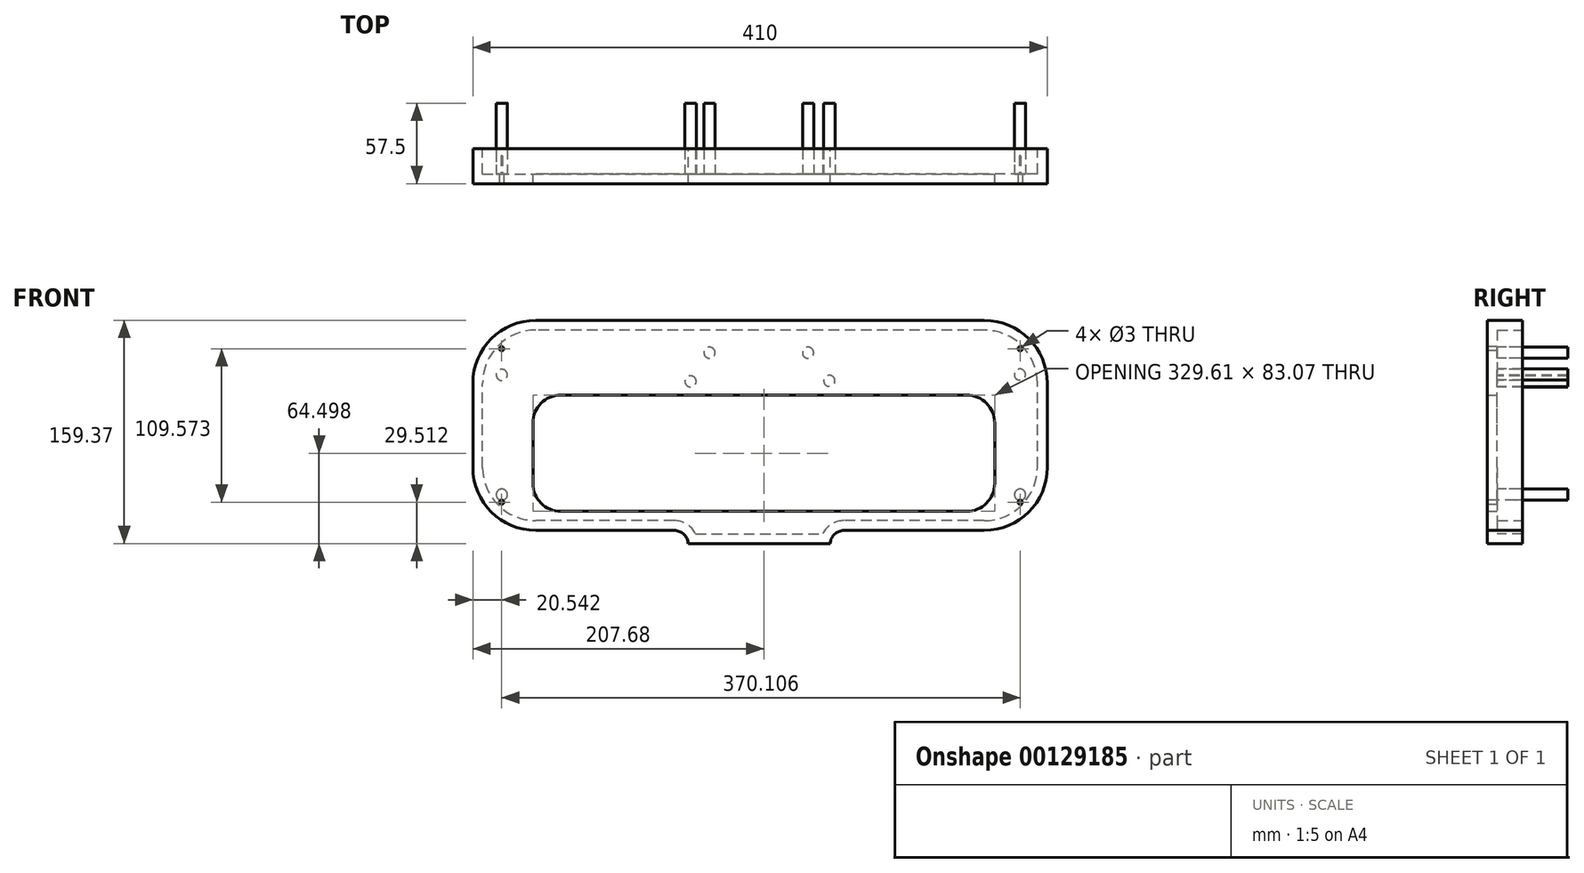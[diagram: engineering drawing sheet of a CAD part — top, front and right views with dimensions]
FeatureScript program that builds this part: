
annotation { "Feature Type Name" : "Feature", "Feature Type Description" : "" }
export const myFeature = defineFeature(function(context is Context, id is Id, definition is map)
    precondition{}
    {
        {
            var Q0;
            Q0=qCreatedBy(makeId("Front.planeOp"),FACE);
            var sketch = newSketch(context, id + "F0", { "sketchPlane" : qUnion([Q0])});
            skLineSegment(sketch, "E0.bottom", {"start": v(205, -75) * mm, "end": v(-205, -75) * mm});
            skLineSegment(sketch, "E0.top", {"start": v(205, 75) * mm, "end": v(-205, 75) * mm});
            skLineSegment(sketch, "E0.left", {"start": v(205, -75) * mm, "end": v(205, 75) * mm});
            skLineSegment(sketch, "E0.right", {"start": v(-205, -75) * mm, "end": v(-205, 75) * mm});
            skSolve(sketch);
        }
        {
            var Q0;
            Q0=qSketchRegion(id+"F0",true);
            extrude(context, id + "F1", {"entities" : qUnion([Q0]), "depth" : 5 * mm, "hasSecondDirection" : true, "secondDirectionOppositeDirection" : true, "secondDirectionDepth" : 20 * mm});
        }
        {
            var Q0;
            Q0=makeQuery(id+"F1.opExtrude","SWEPT_EDGE",EDGE,{"disambiguationData":[OSD([sQuery(id+"F0.wireOp",EDGE,"E0.top"),sQuery(id+"F0.wireOp",EDGE,"E0.right")])]});
            var Q1;
            Q1=makeQuery(id+"F1.opExtrude","SWEPT_EDGE",EDGE,{"disambiguationData":[OSD([sQuery(id+"F0.wireOp",EDGE,"E0.bottom"),sQuery(id+"F0.wireOp",EDGE,"E0.right")])]});
            fillet(context, id + "F2", {"entities" : qUnion([Q0, Q1]), "radius" : 45 * mm, "tangentPropagation" : true, "allowEdgeOverflow" : false});
        }
        {
            var Q0;
            Q0=makeQuery(id+"F1.opExtrude","SWEPT_EDGE",EDGE,{"disambiguationData":[OSD([sQuery(id+"F0.wireOp",EDGE,"E0.top"),sQuery(id+"F0.wireOp",EDGE,"E0.left")])]});
            fillet(context, id + "F3", {"entities" : qUnion([Q0]), "radius" : 45 * mm, "tangentPropagation" : true, "allowEdgeOverflow" : false});
        }
        {
            var Q0;
            Q0=makeQuery(id+"F1.opExtrude","SWEPT_EDGE",EDGE,{"disambiguationData":[OSD([sQuery(id+"F0.wireOp",EDGE,"E0.bottom"),sQuery(id+"F0.wireOp",EDGE,"E0.left")])]});
            fillet(context, id + "F4", {"entities" : qUnion([Q0]), "radius" : 45 * mm, "tangentPropagation" : true, "allowEdgeOverflow" : false});
        }
        {
            var Q0;
            Q0=qCreatedBy(makeId("Front.planeOp"),FACE);
            var sketch = newSketch(context, id + "F5", { "sketchPlane" : qUnion([Q0])});
            skLineSegment(sketch, "E1.bottom", {"start": v(-51.28, -63.48) * mm, "end": v(50, -63.48) * mm});
            skLineSegment(sketch, "E1.top", {"start": v(-51.28, -84.37) * mm, "end": v(50, -84.37) * mm});
            skLineSegment(sketch, "E1.left", {"start": v(-51.28, -63.48) * mm, "end": v(-51.28, -84.37) * mm});
            skLineSegment(sketch, "E1.right", {"start": v(50, -63.48) * mm, "end": v(50, -84.37) * mm});
            skSolve(sketch);
        }
        {
            var Q0;
            Q0=qSketchRegion(id+"F5",true);
            extrude(context, id + "F6", {"entities" : qUnion([Q0]), "operationType" : NewBodyOperationType.ADD, "depth" : 5 * mm, "hasSecondDirection" : true, "secondDirectionOppositeDirection" : true, "secondDirectionDepth" : 20 * mm});
        }
        {
            var Q0;
            Q0=makeQuery(id+"F6.boolean.opBoolean","INTERSECT",EDGE,{"derivedFrom":[makeQuery(id+"F1.opExtrude","SWEPT_FACE",FACE,{"disambiguationData":[OSD([sQuery(id+"F0.wireOp",EDGE,"E0.bottom")])]}),makeQuery(id+"F6.opExtrude","SWEPT_FACE",FACE,{"disambiguationData":[OSD([sQuery(id+"F5.wireOp",EDGE,"E1.left")])]})]});
            fillet(context, id + "F7", {"entities" : qUnion([Q0]), "radius" : 10 * mm, "tangentPropagation" : true, "allowEdgeOverflow" : false});
        }
        {
            var Q0;
            Q0=makeQuery(id+"F6.boolean.opBoolean","INTERSECT",EDGE,{"derivedFrom":[makeQuery(id+"F1.opExtrude","SWEPT_FACE",FACE,{"disambiguationData":[OSD([sQuery(id+"F0.wireOp",EDGE,"E0.bottom")])]}),makeQuery(id+"F6.opExtrude","SWEPT_FACE",FACE,{"disambiguationData":[OSD([sQuery(id+"F5.wireOp",EDGE,"E1.right")])]})]});
            fillet(context, id + "F8", {"entities" : qUnion([Q0]), "radius" : 10 * mm, "tangentPropagation" : true, "allowEdgeOverflow" : false});
        }
        {
            var Q0;
            Q0=makeQuery(id+"F6.boolean.opBoolean","MERGE",FACE,{"derivedFrom":[makeQuery(id+"F1.opExtrude","CAP_FACE",FACE,{"disambiguationData":[OSD([sQuery(id+"F0.wireOp",EDGE,"E0.bottom"),sQuery(id+"F0.wireOp",EDGE,"E0.top"),sQuery(id+"F0.wireOp",EDGE,"E0.left"),sQuery(id+"F0.wireOp",EDGE,"E0.right")])],"isStart":false}),makeQuery(id+"F6.opExtrude","CAP_FACE",FACE,{"disambiguationData":[OSD([sQuery(id+"F5.wireOp",EDGE,"E1.bottom"),sQuery(id+"F5.wireOp",EDGE,"E1.top"),sQuery(id+"F5.wireOp",EDGE,"E1.left"),sQuery(id+"F5.wireOp",EDGE,"E1.right")])],"isStart":false})]});
            cPlane(context, id + "F9", {"entities" : qUnion([Q0]), "cplaneType" : CPlaneType.OFFSET, "offset" : 0 * mm, "width" : 150 * mm, "height" : 150 * mm});
        }
        {
            var Q0;
            Q0=makeQuery(id+"F1.opExtrude","CAP_FACE",FACE,{"disambiguationData":[OSD([sQuery(id+"F0.wireOp",EDGE,"E0.bottom"),sQuery(id+"F0.wireOp",EDGE,"E0.top"),sQuery(id+"F0.wireOp",EDGE,"E0.left"),sQuery(id+"F0.wireOp",EDGE,"E0.right")])],"isStart":true});
            shell(context, id + "F10", {"entities" : qUnion([Q0]), "thickness" : 7 * mm});
        }
        {
            var Q0;
            Q0=makeQuery(id+"F6.boolean.opBoolean","MERGE",FACE,{"derivedFrom":[makeQuery(id+"F1.opExtrude","CAP_FACE",FACE,{"disambiguationData":[OSD([sQuery(id+"F0.wireOp",EDGE,"E0.bottom"),sQuery(id+"F0.wireOp",EDGE,"E0.top"),sQuery(id+"F0.wireOp",EDGE,"E0.left"),sQuery(id+"F0.wireOp",EDGE,"E0.right")])],"isStart":false}),makeQuery(id+"F6.opExtrude","CAP_FACE",FACE,{"disambiguationData":[OSD([sQuery(id+"F5.wireOp",EDGE,"E1.bottom"),sQuery(id+"F5.wireOp",EDGE,"E1.top"),sQuery(id+"F5.wireOp",EDGE,"E1.left"),sQuery(id+"F5.wireOp",EDGE,"E1.right")])],"isStart":false})]});
            cPlane(context, id + "F11", {"entities" : qUnion([Q0]), "cplaneType" : CPlaneType.OFFSET, "offset" : 2 * mm, "oppositeDirection" : true, "width" : 150 * mm, "height" : 150 * mm});
        }
        {
            var Q0;
            Q0=qCreatedBy(id+"F11.planeOp",FACE);
            var sketch = newSketch(context, id + "F12", { "sketchPlane" : qUnion([Q0])});
            skCircle(sketch, "E2", {"center": v(-184.3, 36.01) * mm, "radius": 4 * mm});
            skCircle(sketch, "E3", {"center": v(-184.28, -49.46) * mm, "radius": 4 * mm});
            skCircle(sketch, "E4", {"center": v(-36.07, 51.83) * mm, "radius": 4 * mm});
            skCircle(sketch, "E5", {"center": v(-49.57, 31.39) * mm, "radius": 4 * mm});
            skCircle(sketch, "E6", {"center": v(34.27, 51.83) * mm, "radius": 4 * mm});
            skCircle(sketch, "E7", {"center": v(49.46, 31.76) * mm, "radius": 4 * mm});
            skCircle(sketch, "E8", {"center": v(185.45, 36.26) * mm, "radius": 4 * mm});
            skCircle(sketch, "E9", {"center": v(185.64, -49.46) * mm, "radius": 4 * mm});
            skSolve(sketch);
        }
        {
            var Q0;
            Q0 = qSketchRegion(id + "F12", true);
            extrude(context, id + "F13", {"entities" : qUnion([Q0]), "operationType" : NewBodyOperationType.ADD, "oppositeDirection" : true, "depth" : 55.5 * mm});
        }
        {
            var Q0;
            Q0=makeQuery(id+"F0.imprint","IMPRINT",FACE,{"disambiguationData":[TD([[makeQuery(id+"F0.imprint","IMPRINT",EDGE,{"derivedFrom":sQuery(id+"F0.wireOp",EDGE,"E0.bottom")}),-1.0]])]});
            var sketch = newSketch(context, id + "F14", { "sketchPlane" : qUnion([Q0])});
            skLineSegment(sketch, "E10.bottom", {"start": v(167.49, 21.66) * mm, "end": v(-162.13, 21.66) * mm});
            skLineSegment(sketch, "E10.top", {"start": v(167.49, -61.4) * mm, "end": v(-162.13, -61.4) * mm});
            skLineSegment(sketch, "E10.left", {"start": v(167.49, 21.66) * mm, "end": v(167.49, -61.4) * mm});
            skLineSegment(sketch, "E10.right", {"start": v(-162.13, 21.66) * mm, "end": v(-162.13, -61.4) * mm});
            skSolve(sketch);
        }
        {
            var Q0;
            Q0 = qSketchRegion(id + "F14", true);
            extrude(context, id + "F15", {"entities" : qUnion([Q0]), "operationType" : NewBodyOperationType.REMOVE, "depth" : 25 * mm, "hasSecondDirection" : true, "secondDirectionOppositeDirection" : true, "secondDirectionDepth" : 25 * mm});
        }
        {
            var Q0;
            Q0=makeQuery(id+"F15.boolean.opBoolean","COPY",EDGE,{"derivedFrom":makeQuery(id+"F15.opExtrude","SWEPT_EDGE",EDGE,{"disambiguationData":[OSD([sQuery(id+"F14.wireOp",EDGE,"E10.bottom"),sQuery(id+"F14.wireOp",EDGE,"E10.right")])]})});
            var Q1;
            Q1=makeQuery(id+"F15.boolean.opBoolean","COPY",EDGE,{"derivedFrom":makeQuery(id+"F15.opExtrude","SWEPT_EDGE",EDGE,{"disambiguationData":[OSD([sQuery(id+"F14.wireOp",EDGE,"E10.bottom"),sQuery(id+"F14.wireOp",EDGE,"E10.left")])]})});
            var Q2;
            Q2=makeQuery(id+"F15.boolean.opBoolean","COPY",EDGE,{"derivedFrom":makeQuery(id+"F15.opExtrude","SWEPT_EDGE",EDGE,{"disambiguationData":[OSD([sQuery(id+"F14.wireOp",EDGE,"E10.top"),sQuery(id+"F14.wireOp",EDGE,"E10.left")])]})});
            var Q3;
            Q3=makeQuery(id+"F15.boolean.opBoolean","COPY",EDGE,{"derivedFrom":makeQuery(id+"F15.opExtrude","SWEPT_EDGE",EDGE,{"disambiguationData":[OSD([sQuery(id+"F14.wireOp",EDGE,"E10.top"),sQuery(id+"F14.wireOp",EDGE,"E10.right")])]})});
            fillet(context, id + "F16", {"entities" : qUnion([Q0, Q1, Q2, Q3]), "radius" : 20 * mm, "tangentPropagation" : true, "allowEdgeOverflow" : false});
        }
        {
            var Q0;
            Q0=makeQuery(id+"F13.opExtrude","CAP_FACE",FACE,{"disambiguationData":[OSD([sQuery(id+"F12.wireOp",EDGE,"E8")])],"isStart":false});
            cPlane(context, id + "F17", {"entities" : qUnion([Q0]), "cplaneType" : CPlaneType.OFFSET, "offset" : 0 * mm, "width" : 150 * mm, "height" : 150 * mm});
        }
        {
            var Q0;
            Q0=makeQuery(id+"F6.boolean.opBoolean","MERGE",FACE,{"derivedFrom":[makeQuery(id+"F1.opExtrude","CAP_FACE",FACE,{"disambiguationData":[OSD([sQuery(id+"F0.wireOp",EDGE,"E0.bottom"),sQuery(id+"F0.wireOp",EDGE,"E0.top"),sQuery(id+"F0.wireOp",EDGE,"E0.left"),sQuery(id+"F0.wireOp",EDGE,"E0.right")])],"isStart":false}),makeQuery(id+"F6.opExtrude","CAP_FACE",FACE,{"disambiguationData":[OSD([sQuery(id+"F5.wireOp",EDGE,"E1.bottom"),sQuery(id+"F5.wireOp",EDGE,"E1.top"),sQuery(id+"F5.wireOp",EDGE,"E1.left"),sQuery(id+"F5.wireOp",EDGE,"E1.right")])],"isStart":false})]});
            cPlane(context, id + "F18", {"entities" : qUnion([Q0]), "cplaneType" : CPlaneType.OFFSET, "offset" : 0 * mm, "width" : 150 * mm, "height" : 150 * mm});
        }
        {
            var Q0;
            Q0=qCreatedBy(id+"F18.planeOp",FACE);
            var sketch = newSketch(context, id + "F19", { "sketchPlane" : qUnion([Q0])});
            skLineSegment(sketch, "E11.bottom", {"start": v(-184.46, 54.71) * mm, "end": v(185.65, 54.71) * mm, "construction": true});
            skLineSegment(sketch, "E11.top", {"start": v(-184.46, -54.86) * mm, "end": v(185.65, -54.86) * mm, "construction": true});
            skLineSegment(sketch, "E11.left", {"start": v(-184.46, 54.71) * mm, "end": v(-184.46, -54.86) * mm, "construction": true});
            skLineSegment(sketch, "E11.right", {"start": v(185.65, 54.71) * mm, "end": v(185.65, -54.86) * mm, "construction": true});
            skPoint(sketch, "E12", {"position": v(-184.46, 54.71) * mm});
            skPoint(sketch, "E13", {"position": v(-184.46, -54.86) * mm});
            skPoint(sketch, "E14", {"position": v(185.65, -54.86) * mm});
            skPoint(sketch, "E15", {"position": v(185.65, 54.71) * mm});
            skSolve(sketch);
        }
        {
            var Q0;
            Q0=sQuery(id+"F19.wireOp",VERTEX,"E12");
            var Q1;
            Q1=sQuery(id+"F19.wireOp",VERTEX,"E13");
            var Q2;
            Q2=sQuery(id+"F19.wireOp",VERTEX,"E14");
            var Q3;
            Q3=sQuery(id+"F19.wireOp",VERTEX,"E15");
            var Q4;
            Q4=makeQuery(id+"F1.opExtrude","SWEPT_BODY",BODY,{"disambiguationData":[OSD([sQuery(id+"F0.wireOp",EDGE,"E0.bottom"),sQuery(id+"F0.wireOp",EDGE,"E0.top"),sQuery(id+"F0.wireOp",EDGE,"E0.left"),sQuery(id+"F0.wireOp",EDGE,"E0.right")])]});
            hole(context, id + "F20", {"style" : HoleStyle.SIMPLE, "endStyle" : HoleEndStyle.BLIND, "holeDiameter" : 3 * mm, "holeDepth" : 20 * mm, "locations" : qUnion([Q0, Q1, Q2, Q3]), "scope" : qUnion([Q4])});
        }
    });
